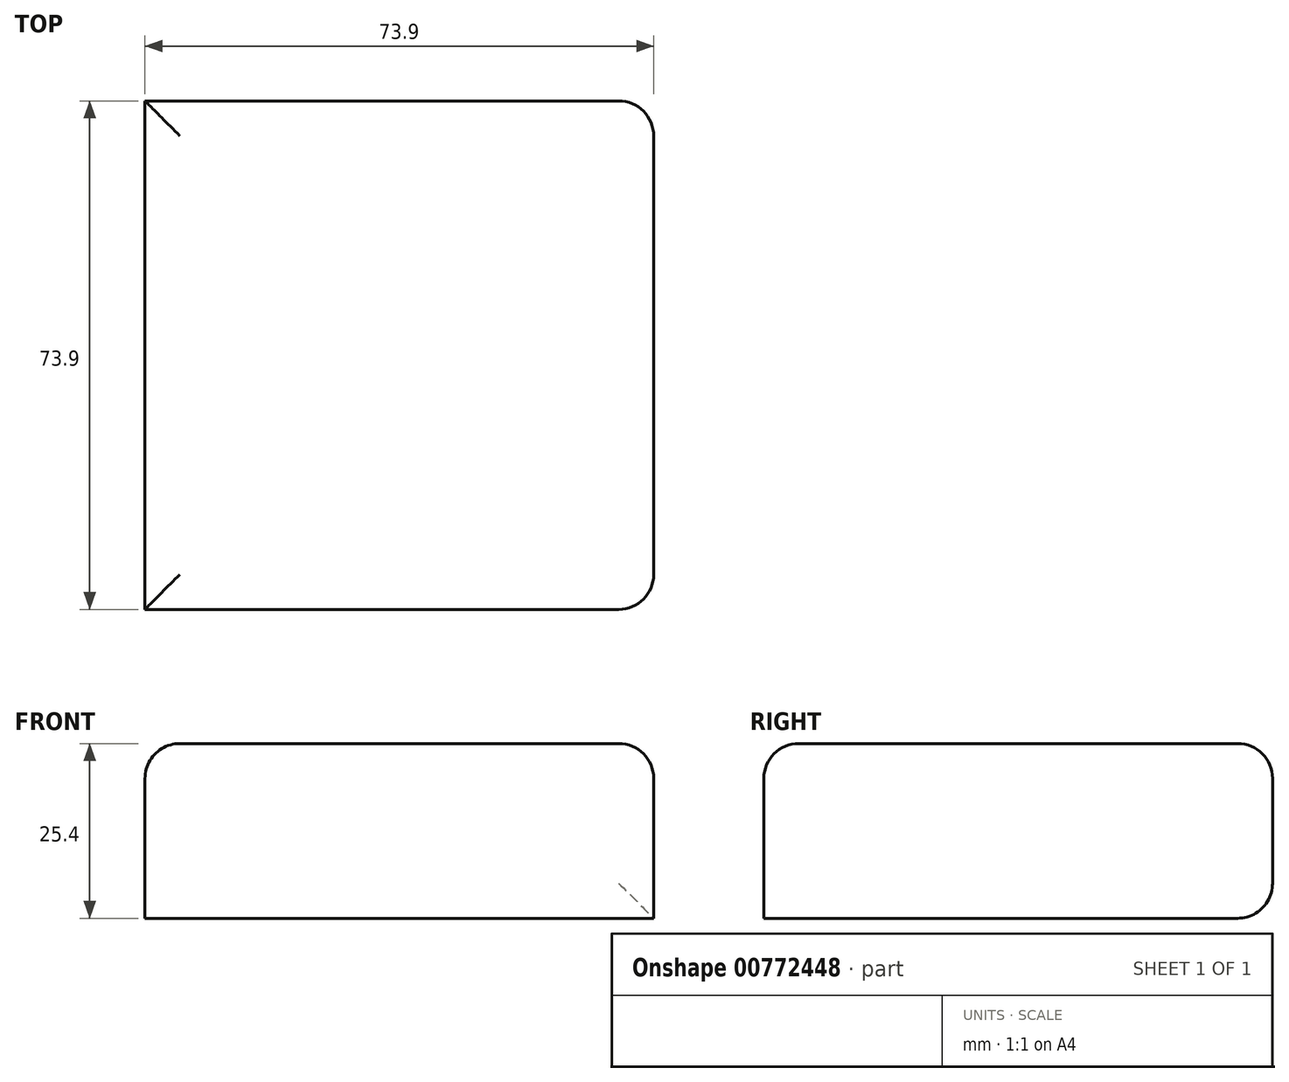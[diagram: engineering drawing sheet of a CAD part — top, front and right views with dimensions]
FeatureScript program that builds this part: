
annotation { "Feature Type Name" : "Feature", "Feature Type Description" : "" }
export const myFeature = defineFeature(function(context is Context, id is Id, definition is map)
    precondition{}
    {
        {
            var Q0;
            Q0=qCreatedBy(makeId("Top.planeOp"),FACE);
            var sketch = newSketch(context, id + "F0", { "sketchPlane" : qUnion([Q0])});
            skLineSegment(sketch, "E0.bottom", {"start": v(-26.11, 42.6) * mm, "end": v(47.8, 42.6) * mm});
            skLineSegment(sketch, "E0.top", {"start": v(-26.11, -31.3) * mm, "end": v(47.8, -31.3) * mm});
            skLineSegment(sketch, "E0.left", {"start": v(-26.11, 42.6) * mm, "end": v(-26.11, -31.3) * mm});
            skLineSegment(sketch, "E0.right", {"start": v(47.8, 42.6) * mm, "end": v(47.8, -31.3) * mm});
            skSolve(sketch);
        }
        {
            var Q0;
            Q0=makeQuery(id+"F0.imprint","IMPRINT",FACE,{"disambiguationData":[TD([[makeQuery(id+"F0.imprint","IMPRINT",EDGE,{"derivedFrom":sQuery(id+"F0.wireOp",EDGE,"E0.bottom")}),-1.0]])]});
            extrude(context, id + "F1", {"entities" : qUnion([Q0]), "depth" : 25.4 * mm, "offsetDistance" : 25.4 * mm});
        }
        {
            var Q0;
            Q0=makeQuery(id+"F1.opExtrude","CAP_EDGE",EDGE,{"disambiguationData":[OSD([sQuery(id+"F0.wireOp",EDGE,"E0.right")])],"isStart":false});
            var Q1;
            Q1=makeQuery(id+"F1.opExtrude","CAP_EDGE",EDGE,{"disambiguationData":[OSD([sQuery(id+"F0.wireOp",EDGE,"E0.top")])],"isStart":false});
            var Q2;
            Q2=makeQuery(id+"F1.opExtrude","CAP_EDGE",EDGE,{"disambiguationData":[OSD([sQuery(id+"F0.wireOp",EDGE,"E0.left")])],"isStart":false});
            var Q3;
            Q3=makeQuery(id+"F1.opExtrude","CAP_EDGE",EDGE,{"disambiguationData":[OSD([sQuery(id+"F0.wireOp",EDGE,"E0.bottom")])],"isStart":false});
            var Q4;
            Q4=makeQuery(id+"F1.opExtrude","CAP_EDGE",EDGE,{"disambiguationData":[OSD([sQuery(id+"F0.wireOp",EDGE,"E0.bottom")])],"isStart":true});
            var Q5;
            Q5=makeQuery(id+"F1.opExtrude","SWEPT_EDGE",EDGE,{"disambiguationData":[OSD([sQuery(id+"F0.wireOp",EDGE,"E0.bottom"),sQuery(id+"F0.wireOp",EDGE,"E0.right")])]});
            var Q6;
            Q6=makeQuery(id+"F1.opExtrude","SWEPT_EDGE",EDGE,{"disambiguationData":[OSD([sQuery(id+"F0.wireOp",EDGE,"E0.top"),sQuery(id+"F0.wireOp",EDGE,"E0.right")])]});
            fillet(context, id + "F2", {"entities" : qUnion([Q0, Q1, Q2, Q3, Q4, Q5, Q6]), "radius" : 5.08 * mm, "tangentPropagation" : true, "allowEdgeOverflow" : false});
        }
    });
